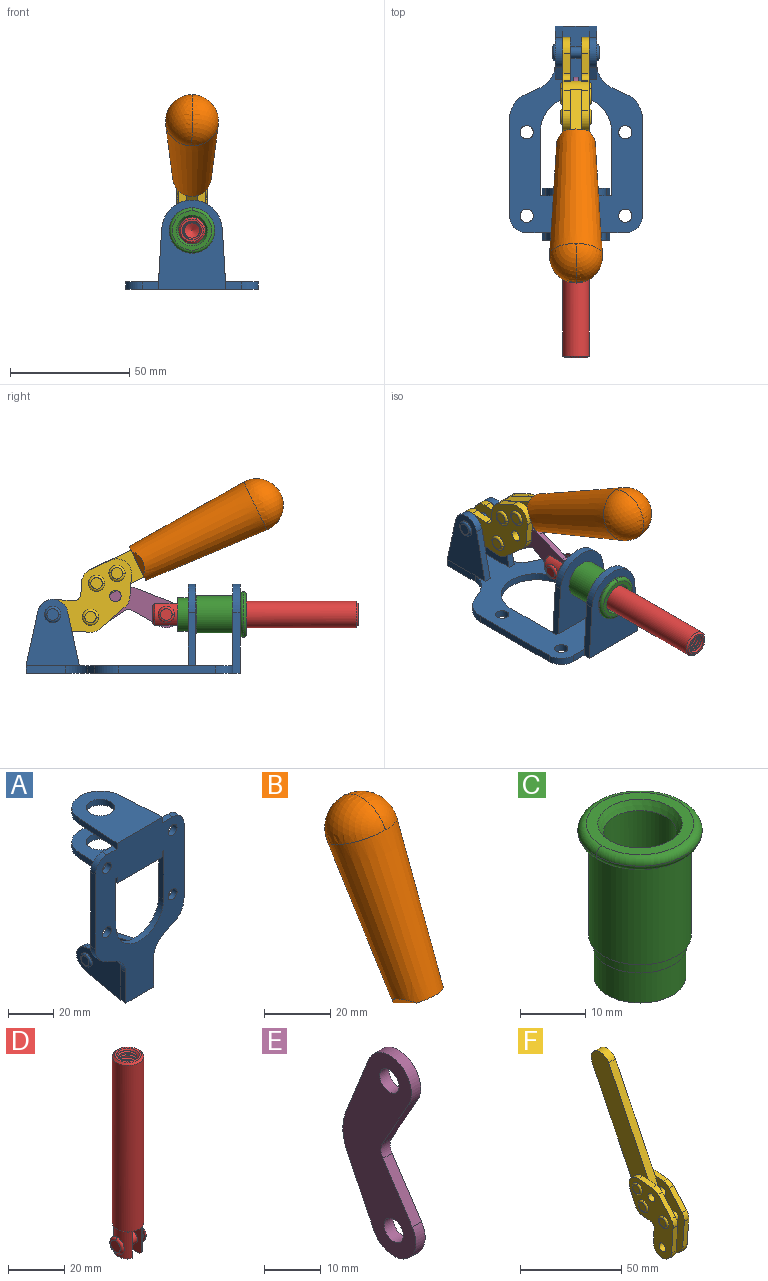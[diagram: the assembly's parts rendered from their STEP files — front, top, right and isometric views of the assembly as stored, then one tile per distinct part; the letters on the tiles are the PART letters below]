
ASSEMBLY  parts=6 mates=6
PART A: 55 faces, bbox 55.7x37.4x89.8 mm
  f0: torus R=2.41mm, axis (-1,0,0), area 15mm2, adj f11,f15,f25
  f1: torus R=2.41mm, axis (-1,0,0), area 15mm2, adj f10,f12,f22
  f2: cylinder r=2.78mm len=5.56mm, axis (0,-1,0), area 54.2mm2, adj f30,f54
  f3: cylinder r=14.99mm len=29.97mm, axis (0,-1,0), area 145.9mm2, adj f30,f49,f53,f54
  f4: cylinder r=2.78mm len=5.56mm, axis (0,-1,0), area 54.2mm2, adj f30,f54
  f5: cylinder r=2.78mm len=5.56mm, axis (0,-1,0), area 54.2mm2, adj f30,f54
  f6: cylinder r=2.78mm len=5.56mm, axis (0,-1,0), area 54.2mm2, adj f30,f54
  f7: cylinder r=6.35mm len=12.7mm, axis (0,0,1), area 123.6mm2, adj f27,f51
  f8: cylinder r=6.35mm len=12.7mm, axis (0,0,-1), area 124.7mm2, adj f21,f35
  f9: cylinder r=2.41mm len=11.18mm, axis (-1,0,0), area 169.4mm2, adj f16,f19
  f10: plane 4.83x4.83mm, normal (1,0,0), area 18.3mm2, adj f1,f12
  f11: plane 4.83x4.83mm, normal (-1,0,0), area 18.3mm2, adj f0,f15
  f12: torus R=2.41mm, axis (-1,0,0), area 15mm2, adj f1,f10,f22
  f13: cylinder r=6.35mm len=12.41mm, axis (1,0,0), area 53.4mm2, adj f18,f19,f22,f23
  f14: cylinder r=6.35mm len=12.41mm, axis (-1,0,0), area 53.4mm2, adj f16,f17,f24,f25
  f15: torus R=2.41mm, axis (-1,0,0), area 15mm2, adj f0,f11,f25
  f16: plane 27.86x22.35mm, normal (1,0,0), area 425.4mm2, adj f9,f14,f17,f24,f30
  f17: plane 22.86x4.97mm, normal (0,0.21,0.98), area 72.5mm2, adj f14,f16,f25,f30
  f18: plane 22.86x4.97mm, normal (0,0.21,0.98), area 72.5mm2, adj f13,f19,f22,f30
  f19: plane 27.86x22.35mm, normal (-1,0,0), area 425.4mm2, adj f9,f13,f18,f23,f30
  f20: cylinder r=12.7mm len=25.35mm, axis (0,0,-1), area 119.8mm2, adj f21,f34,f35,f36
  f21: plane 34.21x28.07mm, normal (0,0,-1), area 702.4mm2, adj f8,f20,f30,f34,f36
  f22: plane 27.96x22.45mm, normal (1,0,0), area 407.2mm2, adj f1,f12,f13,f18,f23,f30,f42,f43
  f23: plane 22.86x4.97mm, normal (0,0.21,-0.98), area 72.5mm2, adj f13,f19,f22,f44
  f24: plane 22.86x4.97mm, normal (0,0.21,-0.98), area 72.5mm2, adj f14,f16,f25,f44
  f25: plane 27.86x22.35mm, normal (-1,0,0), area 407.1mm2, adj f0,f14,f15,f17,f24,f30,f45,f46
  f26: plane 3.1x0.95mm, normal (0,0,-1), area 2.7mm2, adj f30,f49,f50,f54
  f27: plane 34.21x28.07mm, normal (0,0,1), area 702.4mm2, adj f7,f28,f30,f50,f52
  f28: cylinder r=12.7mm len=25.35mm, axis (0,0,1), area 118.8mm2, adj f27,f50,f51,f52
  f29: plane 3.1x0.95mm, normal (0,0,-1), area 2.7mm2, adj f30,f52,f53,f54
  f30: plane 86.54x55.63mm, normal (0,1,0), area 2362.9mm2, adj f2,f3,f4,f5,f6,f16,f17,f18
  f31: plane 40.56x3.1mm, normal (-1,0,0), area 125.7mm2, adj f30,f32,f48,f54
  f32: cylinder r=7.11mm len=7.11mm, axis (0,-1,0), area 34.6mm2, adj f30,f31,f33,f54
  f33: plane 6.67x3.1mm, normal (0,0,1), area 20.4mm2, adj f30,f32,f34,f54
  f34: plane 25.39x3.13mm, normal (-1,0.06,0), area 79.5mm2, adj f20,f21,f33,f35,f54
  f35: plane 37.31x28.45mm, normal (0,0,1), area 789.9mm2, adj f8,f20,f34,f36,f54
  f36: plane 25.39x3.13mm, normal (1,0.06,0), area 79.5mm2, adj f20,f21,f35,f37,f54
  f37: plane 6.67x3.1mm, normal (0,0,1), area 20.4mm2, adj f30,f36,f38,f54
  f38: cylinder r=7.11mm len=7.11mm, axis (0,-1,0), area 34.6mm2, adj f30,f37,f39,f54
  f39: plane 40.56x3.1mm, normal (1,0,0), area 125.7mm2, adj f30,f38,f40,f54
  f40: cylinder r=11.18mm len=10.16mm, axis (0,-1,0), area 39.5mm2, adj f30,f39,f41,f54
  f41: plane 6.09x3.1mm, normal (0.42,0,-0.91), area 20.8mm2, adj f30,f40,f42,f54
  f42: cylinder r=11.18mm len=9.41mm, axis (0,-1,0), area 37.2mm2, adj f22,f30,f41,f43,f54
  f43: plane 16.5x3.1mm, normal (1,0,0), area 51.1mm2, adj f22,f42,f44,f54
  f44: plane 17.37x3.1mm, normal (0,0,-1), area 53.8mm2, adj f23,f24,f30,f43,f45,f54
  f45: plane 16.5x3.1mm, normal (-1,0,0), area 51.1mm2, adj f25,f44,f46,f54
  f46: cylinder r=11.18mm len=9.41mm, axis (0,-1,0), area 37.2mm2, adj f25,f30,f45,f47,f54
  f47: plane 6.09x3.1mm, normal (-0.42,0,-0.91), area 20.8mm2, adj f30,f46,f48,f54
  f48: cylinder r=11.18mm len=10.16mm, axis (0,-1,0), area 39.5mm2, adj f30,f31,f47,f54
  f49: plane 26.54x3.1mm, normal (-1,0,0), area 82.3mm2, adj f3,f26,f30,f54
  f50: plane 25.39x3.1mm, normal (1,0.06,0), area 78.8mm2, adj f26,f27,f28,f51,f54
  f51: plane 37.31x28.45mm, normal (0,0,-1), area 789.9mm2, adj f7,f28,f50,f52,f54
  f52: plane 25.39x3.1mm, normal (-1,0.06,0), area 78.8mm2, adj f27,f28,f29,f51,f54
  f53: plane 26.54x3.1mm, normal (1,0,0), area 82.3mm2, adj f3,f29,f30,f54
  f54: plane 89.66x55.63mm, normal (0,-1,0), area 2678.5mm2, adj f2,f3,f4,f5,f6,f26,f29,f31
PART B: 11 faces, bbox 22.3x42.6x64.5 mm
  f0: sphere r=11.13mm, area 411.4mm2, adj f1,f8
  f1: cone r=11.11mm half-angle=3.3deg, axis (0,0.44,0.9), area 3251.8mm2, adj f0,f7,f8,f9,f10
  f2: cylinder r=6.16mm len=11.7mm, axis (1,0,0), area 89.5mm2, adj f3,f4,f5,f6
  f3: plane 60.23x36.75mm, normal (-1,0,0), area 763.6mm2, adj f2,f4,f6,f10
  f4: plane 51.37x25.05mm, normal (0,0.9,-0.44), area 264.2mm2, adj f2,f3,f5,f10
  f5: plane 60.23x36.75mm, normal (1,0,0), area 763.6mm2, adj f2,f4,f6,f10
  f6: plane 51.37x25.05mm, normal (0,-0.9,0.44), area 264.2mm2, adj f2,f3,f5,f10
  f7: plane 9.95x5.95mm, normal (0.71,-0.31,-0.64), area 25.8mm2, adj f1,f10
  f8: sphere r=11.13mm, area 411.4mm2, adj f0,f1
  f9: plane 9.95x5.95mm, normal (-0.71,-0.31,-0.64), area 25.8mm2, adj f1,f10
  f10: plane 14.27x11.38mm, normal (0,-0.44,-0.9), area 106.7mm2, adj f1,f3,f4,f5,f6,f7,f9
PART C: 15 faces, bbox 20.6x20.6x28.7 mm
  f0: torus R=8.26mm, axis (0,0,1), area 56.8mm2, adj f1,f10,f12
  f1: torus R=8.26mm, axis (0,0,1), area 56.8mm2, adj f0,f6,f13
  f2: cylinder r=5.59mm len=25.91mm, axis (0,0,1), area 909.6mm2, adj f3,f4
  f3: cone r=6.86mm half-angle=45deg, axis (0,0,-1), area 70.2mm2, adj f2,f14
  f4: cone r=6.47mm half-angle=30deg, axis (0,0,1), area 66.7mm2, adj f2,f13
  f5: cylinder r=7.04mm len=14.07mm, axis (0,0,1), area 252.6mm2, adj f11,f14
  f6: torus R=8.26mm, axis (0,0,1), area 56.8mm2, adj f1,f12,f13
  f7: cylinder r=7.16mm len=14.33mm, axis (0,0,1), area 91.5mm2, adj f9,f11
  f8: cylinder r=7.86mm len=18.42mm, axis (0,0,1), area 909.6mm2, adj f9,f10
  f9: plane 15.72x15.72mm, normal (0,0,-1), area 33mm2, adj f7,f8
  f10: plane 16.51x16.51mm, normal (0,0,-1), area 19.9mm2, adj f0,f8,f12
  f11: plane 14.33x14.33mm, normal (0,0,-1), area 5.7mm2, adj f5,f7
  f12: torus R=8.26mm, axis (0,0,1), area 56.8mm2, adj f0,f6,f10
  f13: plane 16.51x16.51mm, normal (0,0,1), area 82.7mm2, adj f1,f4,f6
  f14: plane 14.07x14.07mm, normal (0,0,-1), area 7.8mm2, adj f3,f5
PART D: 48 faces, bbox 12.6x11.1x86.1 mm
  f0: torus R=2.41mm, axis (-1,0,0), area 15mm2, adj f30,f32,f34
  f1: torus R=2.41mm, axis (-1,0,0), area 15mm2, adj f29,f31,f33
  f2: cylinder r=5.54mm len=72.39mm, axis (0,0,1), area 2518.5mm2, adj f3,f4,f42,f43
  f3: cone r=5.54mm half-angle=45deg, axis (0,0,1), area 7.6mm2, adj f2,f5,f41
  f4: cone r=5.54mm half-angle=45deg, axis (0,0,-1), area 34.9mm2, adj f2,f39
  f5: cylinder r=5.08mm len=11.48mm, axis (0,0,1), area 108.3mm2, adj f3,f7,f8,f41
  f6: cylinder r=2.41mm len=4.83mm, axis (-1,0,0), area 71.2mm2, adj f40,f41
  f7: cylinder r=2.41mm len=4.83mm, axis (-1,0,0), area 7.6mm2, adj f5,f34
  f8: cone r=5.08mm half-angle=45deg, axis (0,0,1), area 10.6mm2, adj f5,f37,f41
  f9: cone r=3.98mm half-angle=45deg, axis (0,0,1), area 17.6mm2, adj f27,f39,f45,f46,f47
  f10: cylinder r=2.41mm len=4.83mm, axis (-1,0,0), area 7.6mm2, adj f33,f38
  f11: cylinder r=3.2mm len=6.4mm, axis (0,0,1), area 78.4mm2, adj f12,f28,f44,f45,f47
  f12: cylinder r=3.2mm len=6.4mm, axis (0,0,1), area 10.5mm2, adj f11,f13,f45,f47
  f13: cylinder r=3.2mm len=6.4mm, axis (0,0,1), area 10.5mm2, adj f12,f14,f45,f47
  f14: cylinder r=3.2mm len=6.4mm, axis (0,0,1), area 10.5mm2, adj f13,f15,f45,f47
  f15: cylinder r=3.2mm len=6.4mm, axis (0,0,1), area 10.5mm2, adj f14,f16,f45,f47
  f16: cylinder r=3.2mm len=6.4mm, axis (0,0,1), area 10.5mm2, adj f15,f17,f45,f47
  f17: cylinder r=3.2mm len=6.4mm, axis (0,0,1), area 10.5mm2, adj f16,f18,f45,f47
  f18: cylinder r=3.2mm len=6.4mm, axis (0,0,1), area 10.5mm2, adj f17,f19,f45,f47
  f19: cylinder r=3.2mm len=6.4mm, axis (0,0,1), area 10.5mm2, adj f18,f20,f45,f47
  f20: cylinder r=3.2mm len=6.4mm, axis (0,0,1), area 10.5mm2, adj f19,f21,f45,f47
  f21: cylinder r=3.2mm len=6.4mm, axis (0,0,1), area 10.5mm2, adj f20,f22,f45,f47
  f22: cylinder r=3.2mm len=6.4mm, axis (0,0,1), area 10.5mm2, adj f21,f23,f45,f47
  f23: cylinder r=3.2mm len=6.4mm, axis (0,0,1), area 10.5mm2, adj f22,f24,f45,f47
  f24: cylinder r=3.2mm len=6.4mm, axis (0,0,1), area 10.5mm2, adj f23,f25,f45,f47
  f25: cylinder r=3.2mm len=6.4mm, axis (0,0,1), area 10.5mm2, adj f24,f26,f45,f47
  f26: cylinder r=3.2mm len=6.4mm, axis (0,0,1), area 10.5mm2, adj f25,f27,f45,f47
  f27: cylinder r=3.2mm len=6.4mm, axis (0,0,1), area 7.4mm2, adj f9,f26,f45,f47
  f28: cone r=3.2mm half-angle=60deg, axis (0,0,1), area 37.2mm2, adj f11
  f29: plane 4.83x4.83mm, normal (-1,0,0), area 18.3mm2, adj f1,f31
  f30: plane 4.83x4.83mm, normal (1,0,0), area 18.3mm2, adj f0,f32
  f31: torus R=2.41mm, axis (-1,0,0), area 15mm2, adj f1,f29,f33
  f32: torus R=2.41mm, axis (-1,0,0), area 15mm2, adj f0,f30,f34
  f33: plane 6.83x6.83mm, normal (1,0,0), area 18.3mm2, adj f1,f10,f31
  f34: plane 6.83x6.83mm, normal (-1,0,0), area 18.3mm2, adj f0,f7,f32
  f35: cone r=5.08mm half-angle=45deg, axis (0,0,1), area 10.6mm2, adj f36,f38,f40
  f36: plane 7.25x1.97mm, normal (0,0,-1), area 10mm2, adj f35,f40
  f37: plane 7.25x1.97mm, normal (0,0,-1), area 10mm2, adj f8,f41
  f38: cylinder r=5.08mm len=11.48mm, axis (0,0,1), area 108.3mm2, adj f10,f35,f40,f42
  f39: plane 9.55x9.55mm, normal (0,0,1), area 22mm2, adj f4,f9
  f40: plane 12.76x10.09mm, normal (1,0,0), area 95.7mm2, adj f6,f35,f36,f38,f42,f43
  f41: plane 12.76x10.09mm, normal (-1,0,0), area 95.7mm2, adj f3,f5,f6,f8,f37,f43
  f42: cone r=5.54mm half-angle=45deg, axis (0,0,1), area 7.6mm2, adj f2,f38,f40
  f43: plane 11.07x4.7mm, normal (0,0,-1), area 50.4mm2, adj f2,f40,f41
  f44: plane 0.89x0.62mm, normal (-1,0,0), area 0.3mm2, adj f11,f45,f46,f47
  f45: bspline ~24.8x7.63mm, area 266.6mm2, adj f9,f11,f12,f13,f14,f15,f16,f17
  f46: bspline ~24.87x7.63mm, area 73.6mm2, adj f9,f44,f45,f47
  f47: bspline ~24.98x7.63mm, area 272.5mm2, adj f9,f11,f12,f13,f14,f15,f16,f17
PART E: 12 faces, bbox 2.3x18.2x42.8 mm
  f0: cylinder r=2.4mm len=4.8mm, axis (1,0,0), area 34.9mm2, adj f4,f11
  f1: cylinder r=10.41mm len=8.47mm, axis (1,0,0), area 20.2mm2, adj f4,f9,f10,f11
  f2: cylinder r=3.05mm len=3.16mm, axis (1,0,0), area 7.7mm2, adj f4,f6,f7,f11
  f3: cylinder r=2.4mm len=4.8mm, axis (1,0,0), area 34.9mm2, adj f4,f11
  f4: plane 42.81x18.23mm, normal (-1,0,0), area 414.1mm2, adj f0,f1,f2,f3,f5,f6,f7,f8
  f5: cylinder r=5.54mm len=10.67mm, axis (1,0,0), area 41.8mm2, adj f4,f6,f10,f11
  f6: plane 11.66x6.53mm, normal (0,-0.87,-0.49), area 30.9mm2, adj f2,f4,f5,f11
  f7: plane 11.17x7.33mm, normal (0,-0.84,0.55), area 30.9mm2, adj f2,f4,f8,f11
  f8: cylinder r=5.54mm len=10.51mm, axis (1,0,0), area 41.8mm2, adj f4,f7,f9,f11
  f9: plane 13.67x6.67mm, normal (0,0.9,-0.44), area 35.1mm2, adj f1,f4,f8,f11
  f10: plane 14.1x5.7mm, normal (0,0.93,0.37), area 35.1mm2, adj f1,f4,f5,f11
  f11: plane 42.81x18.23mm, normal (1,0,0), area 414.1mm2, adj f0,f1,f2,f3,f5,f6,f7,f8
PART F: 59 faces, bbox 12.9x60.2x99.6 mm
  f0: torus R=2.39mm, axis (-1,0,0), area 14.9mm2, adj f20,f43,f51
  f1: torus R=2.39mm, axis (-1,0,0), area 14.9mm2, adj f19,f42,f51
  f2: torus R=2.39mm, axis (-1,0,0), area 14.9mm2, adj f18,f35,f51
  f3: torus R=2.39mm, axis (-1,0,0), area 14.9mm2, adj f14,f17,f23
  f4: torus R=2.39mm, axis (-1,0,0), area 14.9mm2, adj f13,f16,f23
  f5: torus R=2.39mm, axis (-1,0,0), area 14.9mm2, adj f12,f15,f23
  f6: cylinder r=2.39mm len=4.78mm, axis (1,0,0), area 46.5mm2, adj f48,f50,f51
  f7: cylinder r=2.39mm len=4.78mm, axis (1,0,0), area 46.5mm2, adj f50,f51
  f8: cylinder r=6.35mm len=12.68mm, axis (1,0,0), area 61.8mm2, adj f38,f39,f50,f51
  f9: cylinder r=2.39mm len=4.78mm, axis (-1,0,0), area 70.5mm2, adj f46,f50
  f10: cylinder r=2.39mm len=4.78mm, axis (-1,0,0), area 46.5mm2, adj f23,f45,f46
  f11: cylinder r=2.39mm len=4.78mm, axis (-1,0,0), area 46.5mm2, adj f23,f46
  f12: plane 4.78x4.78mm, normal (1,0,0), area 17.9mm2, adj f5,f15
  f13: plane 4.78x4.78mm, normal (1,0,0), area 17.9mm2, adj f4,f16
  f14: plane 4.78x4.78mm, normal (1,0,0), area 17.9mm2, adj f3,f17
  f15: torus R=2.39mm, axis (-1,0,0), area 14.9mm2, adj f5,f12,f23
  f16: torus R=2.39mm, axis (-1,0,0), area 14.9mm2, adj f4,f13,f23
  f17: torus R=2.39mm, axis (-1,0,0), area 14.9mm2, adj f3,f14,f23
  f18: plane 4.78x4.78mm, normal (-1,0,0), area 17.9mm2, adj f2,f35
  f19: plane 4.78x4.78mm, normal (-1,0,0), area 17.9mm2, adj f1,f42
  f20: plane 4.78x4.78mm, normal (-1,0,0), area 17.9mm2, adj f0,f43
  f21: plane 2.26x0.2mm, normal (1,0,0), area 0.2mm2, adj f31,f44
  f22: plane 2.26x0.2mm, normal (-1,0,0), area 0.2mm2, adj f41,f44
  f23: plane 39.37x30.77mm, normal (1,0,0), area 565.5mm2, adj f3,f4,f5,f10,f11,f15,f16,f17
  f24: cylinder r=6.1mm len=4.15mm, axis (-1,0,0), area 14.7mm2, adj f23,f25,f32,f46
  f25: plane 10.25x9.01mm, normal (0,-0.75,0.66), area 42.3mm2, adj f23,f24,f26,f46
  f26: cylinder r=6.35mm len=4.64mm, axis (-1,0,0), area 15.6mm2, adj f23,f25,f27,f46
  f27: plane 15.84x3.1mm, normal (0,-1,-0.07), area 49.2mm2, adj f23,f26,f28,f46
  f28: cylinder r=6.35mm len=12.68mm, axis (-1,0,0), area 61.8mm2, adj f23,f27,f29,f46
  f29: plane 8.11x3.1mm, normal (0,1,0.07), area 25.2mm2, adj f23,f28,f30,f46
  f30: cylinder r=3.05mm len=3.25mm, axis (-1,0,0), area 14.8mm2, adj f23,f29,f31,f46
  f31: plane 5.99x3.1mm, normal (0,0.07,-1), area 18.6mm2, adj f21,f23,f30,f44,f46
  f32: plane 9.5x3.1mm, normal (0,-0.07,1), area 29.5mm2, adj f23,f24,f33,f46,f47
  f33: cylinder r=6.1mm len=8.63mm, axis (-1,0,0), area 39.1mm2, adj f23,f32,f34,f47
  f34: plane 8.65x3.96mm, normal (0,0.91,-0.42), area 29.5mm2, adj f23,f33,f44,f47
  f35: torus R=2.39mm, axis (-1,0,0), area 14.9mm2, adj f2,f18,f51
  f36: plane 10.25x9.01mm, normal (0,-0.75,0.66), area 42.3mm2, adj f37,f49,f50,f51
  f37: cylinder r=6.35mm len=4.64mm, axis (1,0,0), area 15.6mm2, adj f36,f38,f50,f51
  f38: plane 15.84x3.1mm, normal (0,-1,-0.07), area 49.2mm2, adj f8,f37,f50,f51
  f39: plane 8.11x3.1mm, normal (0,1,0.07), area 25.2mm2, adj f8,f40,f50,f51
  f40: cylinder r=3.05mm len=3.25mm, axis (1,0,0), area 14.8mm2, adj f39,f41,f50,f51
  f41: plane 5.99x3.1mm, normal (0,0.07,-1), area 18.6mm2, adj f22,f40,f44,f50,f51
  f42: torus R=2.39mm, axis (-1,0,0), area 14.9mm2, adj f1,f19,f51
  f43: torus R=2.39mm, axis (-1,0,0), area 14.9mm2, adj f0,f20,f51
  f44: cylinder r=6.35mm len=12.12mm, axis (-1,0,0), area 128.9mm2, adj f21,f22,f23,f31,f34,f41,f46,f47
  f45: plane 2.65x1.35mm, normal (1,0,0), area 1mm2, adj f10,f55
  f46: plane 39.08x20.42mm, normal (-1,0,0), area 412.5mm2, adj f9,f10,f11,f24,f25,f26,f27,f28
  f47: plane 77.62x39.82mm, normal (1,0,0), area 850mm2, adj f32,f33,f34,f44,f53,f54,f55
  f48: plane 2.65x1.35mm, normal (-1,0,0), area 1mm2, adj f6,f55
  f49: cylinder r=6.1mm len=4.15mm, axis (1,0,0), area 14.7mm2, adj f36,f50,f51,f56
  f50: plane 39.08x20.42mm, normal (1,0,0), area 412.5mm2, adj f6,f7,f8,f9,f36,f37,f38,f39
  f51: plane 39.37x30.77mm, normal (-1,0,0), area 565.5mm2, adj f0,f1,f2,f6,f7,f8,f35,f36
  f52: plane 8.65x3.96mm, normal (0,0.91,-0.42), area 29.5mm2, adj f44,f51,f57,f58
  f53: plane 68.49x33.4mm, normal (0,0.9,-0.44), area 358.1mm2, adj f44,f47,f54,f58
  f54: cylinder r=6.35mm len=12.06mm, axis (1,0,0), area 93.7mm2, adj f47,f53,f55,f58
  f55: plane 68.49x33.4mm, normal (0,-0.9,0.44), area 358.1mm2, adj f44,f45,f46,f47,f48,f50,f54,f58
  f56: plane 9.5x3.1mm, normal (0,-0.07,1), area 29.5mm2, adj f49,f50,f51,f57,f58
  f57: cylinder r=6.1mm len=8.63mm, axis (1,0,0), area 39.1mm2, adj f51,f52,f56,f58
  f58: plane 77.62x39.82mm, normal (-1,0,0), area 850mm2, adj f44,f52,f53,f54,f55,f56,f57
PLACE A rot(axis=(1,0,0),90deg) t=(-0.46,7.95,0.11)mm fixed
PLACE B rot(axis=(1,0,0),90deg) t=(-0.46,7.95,0.11)mm
PLACE C rot(axis=(0.58,-0.58,0.58),120deg) t=(24.16,7.95,24.72)mm
PLACE D rot(axis=(1,0,0),90deg) t=(-0.46,7.95,0.11)mm
PLACE E rot(axis=(1,0,0),90deg) t=(-0.46,7.95,0.11)mm
PLACE F rot(axis=(1,0,0),90deg) t=(-0.46,7.95,0.11)mm
MATE revolute D.f6 <-> E.f5  axis (-1,0,0) through (-0.46,-7.53,24.72)mm
MATE fastened C.f2 <-> A.f7  axis (0,-1,0) through (-0.46,-38.45,24.72)mm
MATE slider A.f7 <-> D.f2  axis (0,-1,0) through (-0.46,-38.45,24.72)mm
MATE revolute F.f7 <-> A.f0  axis (-1,0,0) through (-0.46,40.04,24.72)mm
MATE revolute F.f4 <-> E.f3  axis (-1,0,0) through (-0.46,24.2,23.62)mm
MATE fastened F.f54 <-> B.f2  axis (1,0,0) through (-0.46,-46.83,71.15)mm
